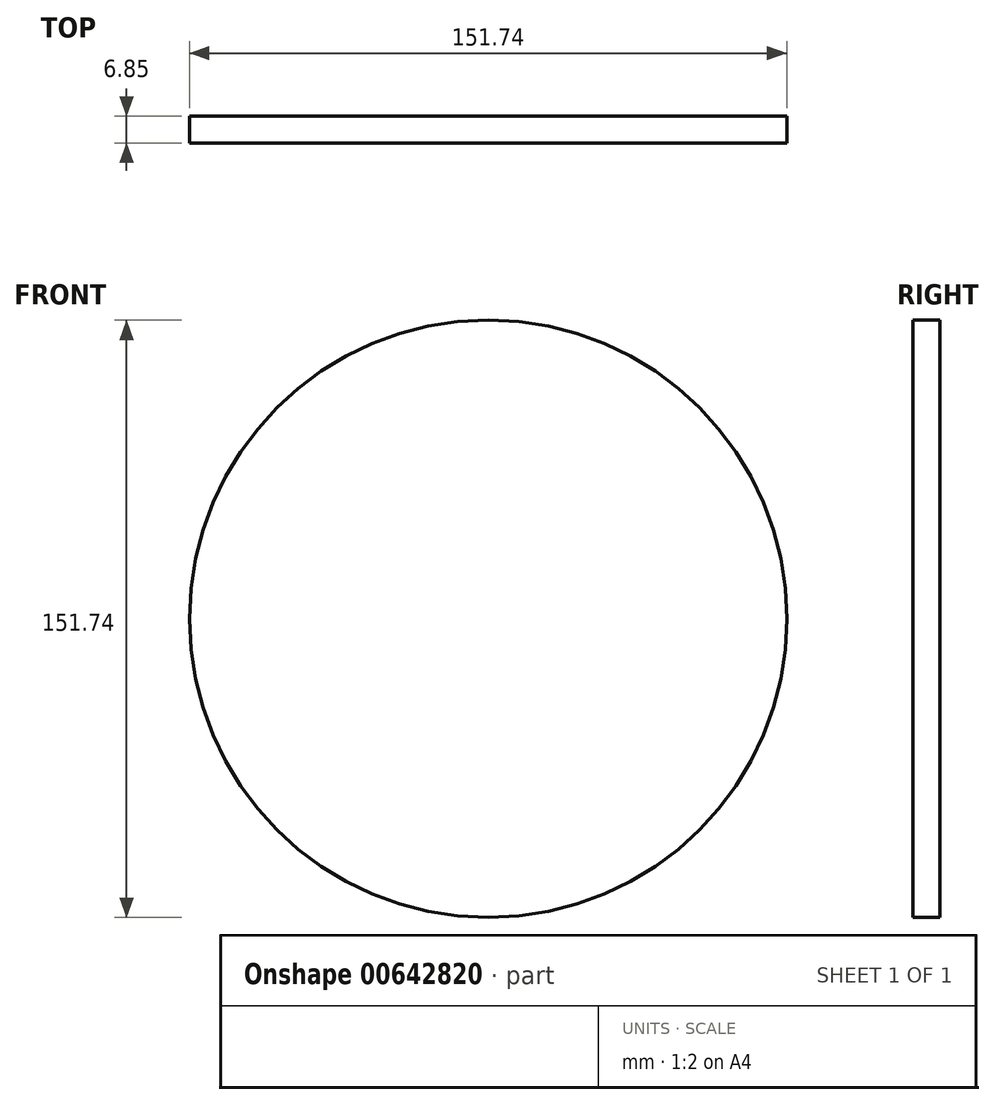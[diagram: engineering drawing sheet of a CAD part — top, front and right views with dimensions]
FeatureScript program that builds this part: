
annotation { "Feature Type Name" : "Feature", "Feature Type Description" : "" }
export const myFeature = defineFeature(function(context is Context, id is Id, definition is map)
    precondition{}
    {
        {
            var Q0;
            Q0=qCreatedBy(makeId("Top.planeOp"),FACE);
            var sketch = newSketch(context, id + "F0", { "sketchPlane" : qUnion([Q0])});
            skLineSegment(sketch, "E0.bottom", {"start": v(-75.87, -75.23) * mm, "end": v(0, -75.23) * mm});
            skLineSegment(sketch, "E0.top", {"start": v(-75.87, -68.38) * mm, "end": v(0, -68.38) * mm});
            skLineSegment(sketch, "E0.left", {"start": v(-75.87, -75.23) * mm, "end": v(-75.87, -68.38) * mm});
            skLineSegment(sketch, "E0.right", {"start": v(0, -75.23) * mm, "end": v(0, -68.38) * mm});
            skLineSegment(sketch, "E1.bottom", {"start": v(-65.23, -68.38) * mm, "end": v(0, -68.38) * mm});
            skLineSegment(sketch, "E1.top", {"start": v(-65.23, -61.26) * mm, "end": v(0, -61.26) * mm});
            skLineSegment(sketch, "E1.left", {"start": v(-65.23, -68.38) * mm, "end": v(-65.23, -61.26) * mm});
            skLineSegment(sketch, "E1.right", {"start": v(0, -68.38) * mm, "end": v(0, -61.26) * mm});
            skLineSegment(sketch, "E2.bottom", {"start": v(-56.3, -61.26) * mm, "end": v(0, -61.26) * mm});
            skLineSegment(sketch, "E2.top", {"start": v(-56.3, -53.1) * mm, "end": v(0, -53.1) * mm});
            skLineSegment(sketch, "E2.left", {"start": v(-56.3, -61.26) * mm, "end": v(-56.3, -53.1) * mm});
            skLineSegment(sketch, "E2.right", {"start": v(0, -61.26) * mm, "end": v(0, -53.1) * mm});
            skLineSegment(sketch, "E3.bottom", {"start": v(-46.52, -53.1) * mm, "end": v(0, -53.1) * mm});
            skLineSegment(sketch, "E3.top", {"start": v(-46.52, -46.38) * mm, "end": v(0, -46.38) * mm});
            skLineSegment(sketch, "E3.left", {"start": v(-46.52, -53.1) * mm, "end": v(-46.52, -46.38) * mm});
            skLineSegment(sketch, "E3.right", {"start": v(0, -53.1) * mm, "end": v(0, -46.38) * mm});
            skLineSegment(sketch, "E4.bottom", {"start": v(-40.02, -46.38) * mm, "end": v(0, -46.38) * mm});
            skLineSegment(sketch, "E4.top", {"start": v(-40.02, -38.83) * mm, "end": v(0, -38.83) * mm});
            skLineSegment(sketch, "E4.left", {"start": v(-40.02, -46.38) * mm, "end": v(-40.02, -38.83) * mm});
            skLineSegment(sketch, "E4.right", {"start": v(0, -46.38) * mm, "end": v(0, -38.83) * mm});
            skLineSegment(sketch, "E5.bottom", {"start": v(-25.36, -38.83) * mm, "end": v(0, -38.83) * mm});
            skLineSegment(sketch, "E5.top", {"start": v(-25.36, -31.9) * mm, "end": v(0, -31.9) * mm});
            skLineSegment(sketch, "E5.left", {"start": v(-25.36, -38.83) * mm, "end": v(-25.36, -31.9) * mm});
            skLineSegment(sketch, "E5.right", {"start": v(0, -38.83) * mm, "end": v(0, -31.9) * mm});
            skLineSegment(sketch, "E6.bottom", {"start": v(-16.31, -31.9) * mm, "end": v(0, -31.9) * mm});
            skLineSegment(sketch, "E6.top", {"start": v(-16.31, -23.88) * mm, "end": v(0, -23.88) * mm});
            skLineSegment(sketch, "E6.left", {"start": v(-16.31, -31.9) * mm, "end": v(-16.31, -23.88) * mm});
            skLineSegment(sketch, "E6.right", {"start": v(0, -31.9) * mm, "end": v(0, -23.88) * mm});
            skLineSegment(sketch, "E7.bottom", {"start": v(-8.16, -23.88) * mm, "end": v(0, -23.88) * mm});
            skLineSegment(sketch, "E7.top", {"start": v(-8.16, -15.32) * mm, "end": v(0, -15.32) * mm});
            skLineSegment(sketch, "E7.left", {"start": v(-8.16, -23.88) * mm, "end": v(-8.16, -15.32) * mm});
            skLineSegment(sketch, "E7.right", {"start": v(0, -23.88) * mm, "end": v(0, -15.32) * mm});
            skLineSegment(sketch, "E8.bottom", {"start": v(-6.21, -15.32) * mm, "end": v(0, -15.32) * mm});
            skLineSegment(sketch, "E8.top", {"start": v(-6.21, -9.74) * mm, "end": v(0, -9.74) * mm});
            skLineSegment(sketch, "E8.left", {"start": v(-6.21, -15.32) * mm, "end": v(-6.21, -9.74) * mm});
            skLineSegment(sketch, "E8.right", {"start": v(0, -15.32) * mm, "end": v(0, -9.74) * mm});
            skLineSegment(sketch, "E9.bottom", {"start": v(-3.1, -9.74) * mm, "end": v(0, -9.74) * mm});
            skLineSegment(sketch, "E9.top", {"start": v(-3.1, -5.62) * mm, "end": v(0, -5.62) * mm});
            skLineSegment(sketch, "E9.left", {"start": v(-3.1, -9.74) * mm, "end": v(-3.1, -5.62) * mm});
            skLineSegment(sketch, "E9.right", {"start": v(0, -9.74) * mm, "end": v(0, -5.62) * mm});
            skSolve(sketch);
        }
        {
            var Q0;
            Q0=makeQuery(id+"F0.imprint","IMPRINT",FACE,{"disambiguationData":[TD([[makeQuery(id+"F0.imprint","IMPRINT",EDGE,{"derivedFrom":sQuery(id+"F0.wireOp",EDGE,"E0.bottom")}),1.0]])]});
            var Q1;
            Q1=makeQuery(id+"F0.imprint","IMPRINT",FACE,{"disambiguationData":[TD([[makeQuery(id+"F0.imprint","IMPRINT",EDGE,{"derivedFrom":sQuery(id+"F0.wireOp",EDGE,"E1.bottom")}),1.0]])]});
            var Q2;
            Q2=makeQuery(id+"F0.imprint","IMPRINT",FACE,{"disambiguationData":[TD([[makeQuery(id+"F0.imprint","IMPRINT",EDGE,{"derivedFrom":sQuery(id+"F0.wireOp",EDGE,"E2.bottom")}),1.0]])]});
            var Q3;
            Q3=makeQuery(id+"F0.imprint","IMPRINT",FACE,{"disambiguationData":[TD([[makeQuery(id+"F0.imprint","IMPRINT",EDGE,{"derivedFrom":sQuery(id+"F0.wireOp",EDGE,"E3.bottom")}),1.0]])]});
            var Q4;
            Q4=makeQuery(id+"F0.imprint","IMPRINT",FACE,{"disambiguationData":[TD([[makeQuery(id+"F0.imprint","IMPRINT",EDGE,{"derivedFrom":sQuery(id+"F0.wireOp",EDGE,"E4.bottom")}),1.0]])]});
            var Q5;
            Q5=makeQuery(id+"F0.imprint","IMPRINT",FACE,{"disambiguationData":[TD([[makeQuery(id+"F0.imprint","IMPRINT",EDGE,{"derivedFrom":sQuery(id+"F0.wireOp",EDGE,"E5.bottom")}),1.0]])]});
            var Q6;
            Q6=makeQuery(id+"F0.imprint","IMPRINT",FACE,{"disambiguationData":[TD([[makeQuery(id+"F0.imprint","IMPRINT",EDGE,{"derivedFrom":sQuery(id+"F0.wireOp",EDGE,"E6.bottom")}),1.0]])]});
            var Q7;
            Q7=makeQuery(id+"F0.imprint","IMPRINT",FACE,{"disambiguationData":[TD([[makeQuery(id+"F0.imprint","IMPRINT",EDGE,{"derivedFrom":sQuery(id+"F0.wireOp",EDGE,"E7.bottom")}),1.0]])]});
            var Q8;
            Q8=makeQuery(id+"F0.imprint","IMPRINT",FACE,{"disambiguationData":[TD([[makeQuery(id+"F0.imprint","IMPRINT",EDGE,{"derivedFrom":sQuery(id+"F0.wireOp",EDGE,"E9.bottom")}),1.0]])]});
            var Q9;
            Q9=makeQuery(id+"F0.imprint","IMPRINT",FACE,{"disambiguationData":[TD([[makeQuery(id+"F0.imprint","IMPRINT",EDGE,{"derivedFrom":sQuery(id+"F0.wireOp",EDGE,"E8.bottom")}),1.0]])]});
            var Q10;
            Q10=sQuery(id+"F0.wireOp",EDGE,"E0.right");
            revolve(context, id + "F1", {"entities" : qUnion([Q0, Q1, Q2, Q3, Q4, Q5, Q6, Q7, Q8, Q9]), "axis" : qUnion([Q10]), "revolveType" : RevolveType.FULL});
        }
    });
